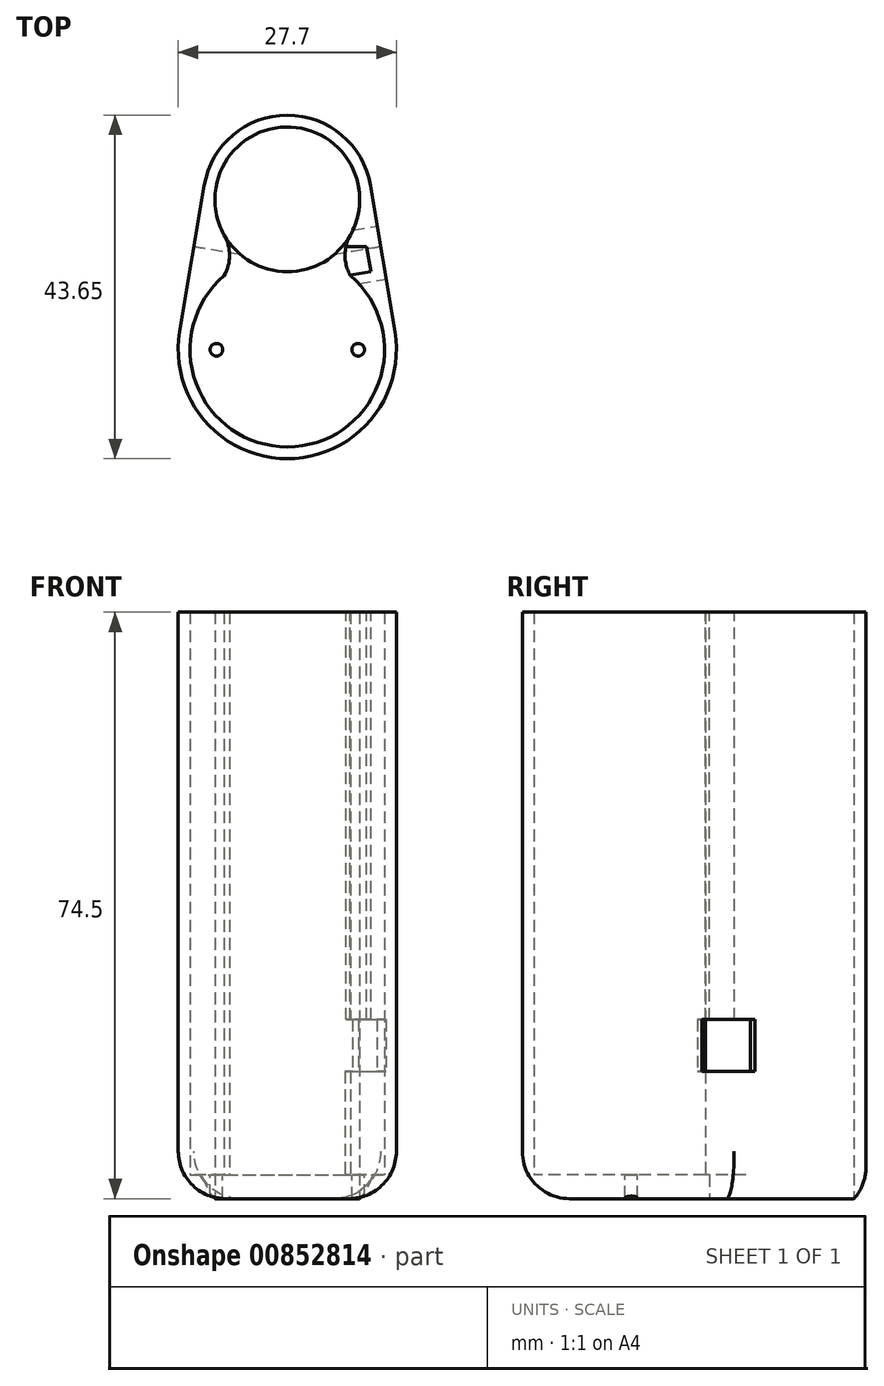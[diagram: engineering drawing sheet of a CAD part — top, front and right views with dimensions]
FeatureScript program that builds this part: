
annotation { "Feature Type Name" : "Feature", "Feature Type Description" : "" }
export const myFeature = defineFeature(function(context is Context, id is Id, definition is map)
    precondition{}
    {
        {
            var Q0;
            Q0=qCreatedBy(makeId("Top.planeOp"),FACE);
            var sketch = newSketch(context, id + "F0", { "sketchPlane" : qUnion([Q0])});
            skLineSegment(sketch, "E0", {"start": v(-8.01, 3.97) * mm, "end": v(8.01, 3.97) * mm});
            skArc(sketch, "E1", {"start": v(-8.01, 3.97) * mm, "mid": v(-10.75, 0.66) * mm, "end": v(-12.18, -3.4) * mm});
            skLineSegment(sketch, "E2", {"start": v(8.01, 3.97) * mm, "end": v(8.01, 3.97) * mm});
            skLineSegment(sketch, "E3", {"start": v(8.01, 9.14) * mm, "end": v(8.01, 9.14) * mm});
            skArc(sketch, "E4", {"start": v(-8.01, 3.97) * mm, "mid": v(-7.33, 6.56) * mm, "end": v(-8.01, 9.14) * mm});
            skLineSegment(sketch, "E5", {"start": v(-8.01, 9.14) * mm, "end": v(-8.01, 9.14) * mm});
            skArc(sketch, "E6", {"start": v(8.01, 9.14) * mm, "mid": v(7.33, 6.56) * mm, "end": v(8.01, 3.97) * mm});
            skArc(sketch, "E7", {"start": v(8.01, 9.14) * mm, "mid": v(8.01, 9.14) * mm, "end": v(8.01, 9.14) * mm});
            skArc(sketch, "E8", {"start": v(8.01, 9.14) * mm, "mid": v(9.06, 12.07) * mm, "end": v(9.07, 15.19) * mm});
            skArc(sketch, "E9", {"start": v(-8.01, 9.14) * mm, "mid": v(0, 4.47) * mm, "end": v(8.01, 9.14) * mm});
            skArc(sketch, "E10", {"start": v(-9.07, 15.19) * mm, "mid": v(-9.06, 12.07) * mm, "end": v(-8.01, 9.14) * mm});
            skLineSegment(sketch, "E11", {"start": v(-9.07, 15.19) * mm, "end": v(-9.07, 15.19) * mm});
            skArc(sketch, "E12", {"start": v(9.07, 15.19) * mm, "mid": v(0, 22.87) * mm, "end": v(-9.07, 15.19) * mm});
            skArc(sketch, "E13", {"start": v(12.18, -3.4) * mm, "mid": v(10.75, 0.66) * mm, "end": v(8.01, 3.97) * mm});
            skArc(sketch, "E14", {"start": v(-12.18, -3.4) * mm, "mid": v(0, -17.78) * mm, "end": v(12.18, -3.4) * mm});
            skLineSegment(sketch, "E15.0", {"start": v(-10.55, 15.43) * mm, "end": v(-13.66, -3.15) * mm});
            skArc(sketch, "E15.1", {"start": v(10.55, 15.43) * mm, "mid": v(0, 24.37) * mm, "end": v(-10.55, 15.43) * mm});
            skLineSegment(sketch, "E15.2", {"start": v(10.55, 15.43) * mm, "end": v(13.66, -3.15) * mm});
            skArc(sketch, "E15.3", {"start": v(-13.66, -3.15) * mm, "mid": v(0, -19.28) * mm, "end": v(13.66, -3.15) * mm});
            skPoint(sketch, "E16", {"position": v(12.35, -5.43) * mm});
            skPoint(sketch, "E17", {"position": v(-12.35, -5.43) * mm});
            skPoint(sketch, "E18", {"position": v(9, -5.43) * mm});
            skPoint(sketch, "E19", {"position": v(-9, -5.43) * mm});
            skLineSegment(sketch, "E20", {"start": v(0, -5.43) * mm, "end": v(0, -4.02) * mm});
            skLineSegment(sketch, "E21", {"start": v(0, -4.02) * mm, "end": v(0, -6.49) * mm});
            skCircle(sketch, "E22", {"center": v(-9, -5.43) * mm, "radius": 0.8 * mm});
            skCircle(sketch, "E23", {"center": v(9, -5.43) * mm, "radius": 0.8 * mm});
            skSolve(sketch);
        }
        {
            var Q0;
            Q0=makeQuery(id+"F0.imprint","IMPRINT",FACE,{"disambiguationData":[TD([[makeQuery(id+"F0.imprint","IMPRINT",EDGE,{"derivedFrom":sQuery(id+"F0.wireOp",EDGE,"E1")}),-1.0]])]});
            extrude(context, id + "F1", {"entities" : qUnion([Q0]), "depth" : 71.5 * mm, "offsetDistance" : 25 * mm});
        }
        {
            var Q0;
            Q0=makeQuery(id+"F0.imprint","IMPRINT",FACE,{"disambiguationData":[TD([[makeQuery(id+"F0.imprint","IMPRINT",EDGE,{"derivedFrom":sQuery(id+"F0.wireOp",EDGE,"E1")}),-1.0]])]});
            var Q1;
            Q1=makeQuery(id+"F0.imprint","IMPRINT",FACE,{"disambiguationData":[TD([[makeQuery(id+"F0.imprint","IMPRINT",EDGE,{"derivedFrom":sQuery(id+"F0.wireOp",EDGE,"E7")}),1.0]])]});
            var Q2;
            Q2=makeQuery(id+"F0.imprint","IMPRINT",FACE,{"disambiguationData":[TD([[makeQuery(id+"F0.imprint","IMPRINT",EDGE,{"derivedFrom":sQuery(id+"F0.wireOp",EDGE,"E0")}),1.0]])]});
            var Q3;
            Q3=makeQuery(id+"F0.imprint","IMPRINT",FACE,{"disambiguationData":[TD([[makeQuery(id+"F0.imprint","IMPRINT",EDGE,{"derivedFrom":sQuery(id+"F0.wireOp",EDGE,"E0")}),-1.0]])]});
            extrude(context, id + "F2", {"entities" : qUnion([Q0, Q1, Q2, Q3]), "operationType" : NewBodyOperationType.ADD, "oppositeDirection" : true, "depth" : 3 * mm, "offsetDistance" : 25 * mm});
        }
        {
            var Q0;
            Q0=makeQuery(id+"F2.opExtrude","CAP_EDGE",EDGE,{"disambiguationData":[OSD([sQuery(id+"F0.wireOp",EDGE,"E15.3")])],"isStart":false});
            fillet(context, id + "F3", {"entities" : qUnion([Q0]), "radius" : 6 * mm, "tangentPropagation" : true, "allowEdgeOverflow" : false});
        }
        {
            var Q0;
            {var subQ0=sQuery(id+"F0.wireOp",EDGE,"E15.2");Q0=makeQuery(id+"F2.boolean.opBoolean","MERGE",FACE,{"derivedFrom":[makeQuery(id+"F1.opExtrude","SWEPT_FACE",FACE,{"disambiguationData":[OSD([subQ0])]}),makeQuery(id+"F2.opExtrude","SWEPT_FACE",FACE,{"disambiguationData":[OSD([subQ0])]})]});}
            var sketch = newSketch(context, id + "F4", { "sketchPlane" : qUnion([Q0])});
            skSolve(sketch);
        }
        {
            var Q0;
            {var subQ0=sQuery(id+"F0.wireOp",EDGE,"E15.2");Q0=makeQuery(id+"F4.imprint","IMPRINT",FACE,{"disambiguationData":[TD([[makeQuery(id+"F4.imprint","IMPRINT",EDGE,{"derivedFrom":makeQuery(id+"F1.opExtrude","CAP_EDGE",EDGE,{"disambiguationData":[OSD([subQ0])],"isStart":false})}),1.0]])]});}
            var sketch = newSketch(context, id + "F5", { "sketchPlane" : qUnion([Q0])});
            skSolve(sketch);
        }
        {
            var Q0;
            {var subQ0=sQuery(id+"F0.wireOp",EDGE,"E15.2");Q0=makeQuery(id+"F5.imprint","IMPRINT",FACE,{"disambiguationData":[TD([[makeQuery(id+"F5.imprint","IMPRINT",EDGE,{"derivedFrom":makeQuery(id+"F4.imprint","IMPRINT",EDGE,{"derivedFrom":makeQuery(id+"F1.opExtrude","CAP_EDGE",EDGE,{"disambiguationData":[OSD([subQ0])],"isStart":false})})}),1.0]])]});}
            var sketch = newSketch(context, id + "F6", { "sketchPlane" : qUnion([Q0])});
            skLineSegment(sketch, "E24.bottom", {"start": v(1.43, 19.76) * mm, "end": v(8.23, 19.76) * mm});
            skLineSegment(sketch, "E24.top", {"start": v(1.43, 13.16) * mm, "end": v(8.23, 13.16) * mm});
            skLineSegment(sketch, "E24.left", {"start": v(1.43, 19.76) * mm, "end": v(1.43, 13.16) * mm});
            skLineSegment(sketch, "E24.right", {"start": v(8.23, 19.76) * mm, "end": v(8.23, 13.16) * mm});
            skPoint(sketch, "E25", {"position": v(4.83, 13.16) * mm});
            skSolve(sketch);
        }
        {
            var Q0;
            Q0=makeQuery(id+"F6.imprint","IMPRINT",FACE,{"disambiguationData":[TD([[makeQuery(id+"F6.imprint","IMPRINT",EDGE,{"derivedFrom":sQuery(id+"F6.wireOp",EDGE,"E24.bottom")}),-1.0]])]});
            extrude(context, id + "F7", {"entities" : qUnion([Q0]), "operationType" : NewBodyOperationType.REMOVE, "oppositeDirection" : true, "depth" : 10 * mm, "offsetDistance" : 25 * mm});
        }
        {
            var Q0;
            Q0=makeQuery(id+"F1.opExtrude","CAP_FACE",FACE,{"disambiguationData":[OSD([sQuery(id+"F0.wireOp",EDGE,"E1"),sQuery(id+"F0.wireOp",EDGE,"E4"),sQuery(id+"F0.wireOp",EDGE,"E6"),sQuery(id+"F0.wireOp",EDGE,"E7"),sQuery(id+"F0.wireOp",EDGE,"E8"),sQuery(id+"F0.wireOp",EDGE,"E10"),sQuery(id+"F0.wireOp",EDGE,"E12"),sQuery(id+"F0.wireOp",EDGE,"E13"),sQuery(id+"F0.wireOp",EDGE,"E14"),sQuery(id+"F0.wireOp",EDGE,"E15.0"),sQuery(id+"F0.wireOp",EDGE,"E15.1"),sQuery(id+"F0.wireOp",EDGE,"E15.2"),sQuery(id+"F0.wireOp",EDGE,"E15.3")])],"isStart":false});
            var sketch = newSketch(context, id + "F8", { "sketchPlane" : qUnion([Q0])});
            skLineSegment(sketch, "E26", {"start": v(6.3, 7.64) * mm, "end": v(10.07, 7.64) * mm});
            skLineSegment(sketch, "E27", {"start": v(10.07, 7.64) * mm, "end": v(10.63, 4.48) * mm});
            skLineSegment(sketch, "E28", {"start": v(10.63, 4.48) * mm, "end": v(6.82, 3.8) * mm});
            skLineSegment(sketch, "E29", {"start": v(6.82, 3.8) * mm, "end": v(6.3, 7.64) * mm});
            skSolve(sketch);
        }
        {
            var Q0;
            {var subQ0=sQuery(id+"F8.wireOp",EDGE,"E27");Q0=makeQuery(id+"F8.imprint","IMPRINT",FACE,{"disambiguationData":[TD([[makeQuery(id+"F8.imprint","IMPRINT",EDGE,{"derivedFrom":subQ0}),-1.0]])]});}
            extrude(context, id + "F9", {"entities" : qUnion([Q0]), "operationType" : NewBodyOperationType.REMOVE, "oppositeDirection" : true, "depth" : 57.4 * mm, "offsetDistance" : 25 * mm});
        }
    });
